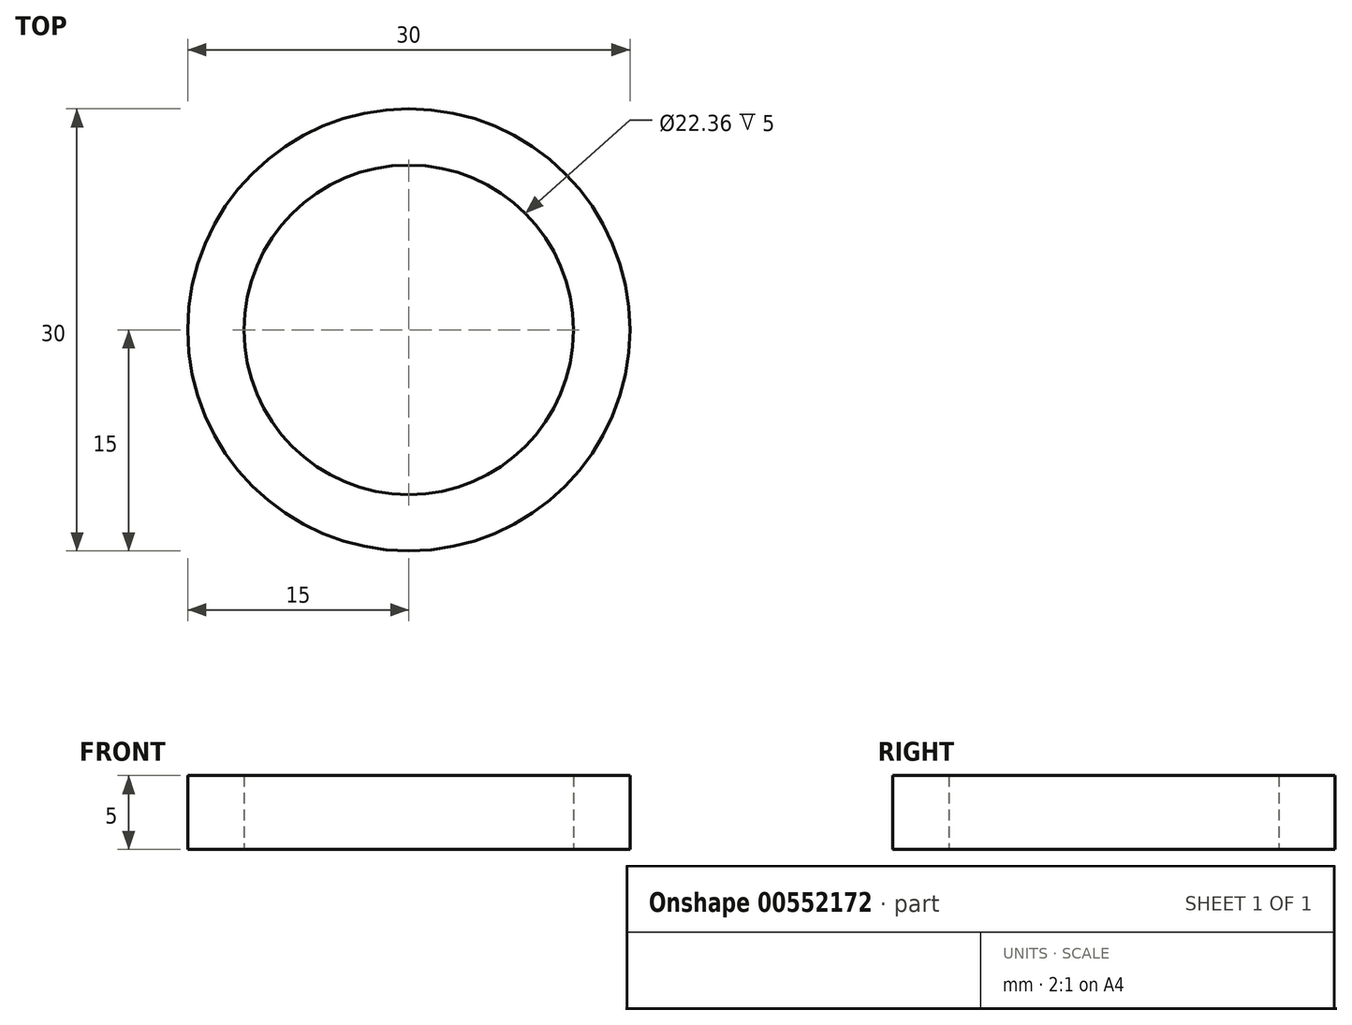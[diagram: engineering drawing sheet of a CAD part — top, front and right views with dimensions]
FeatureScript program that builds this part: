
annotation { "Feature Type Name" : "Feature", "Feature Type Description" : "" }
export const myFeature = defineFeature(function(context is Context, id is Id, definition is map)
    precondition{}
    {
        {
            var Q0;
            Q0=qCreatedBy(makeId("Top.planeOp"),FACE);
            var sketch = newSketch(context, id + "F0", { "sketchPlane" : qUnion([Q0])});
            skCircle(sketch, "E0", {"center": v(0, 0) * mm, "radius": 11.18 * mm});
            skCircle(sketch, "E1", {"center": v(0, 0) * mm, "radius": 15 * mm});
            skSolve(sketch);
        }
        {
            var Q0;
            Q0 = qSketchRegion(id + "F0", true);
            extrude(context, id + "F1", {"entities" : qUnion([Q0]), "depth" : 5 * mm, "offsetDistance" : 25 * mm});
        }
    });
